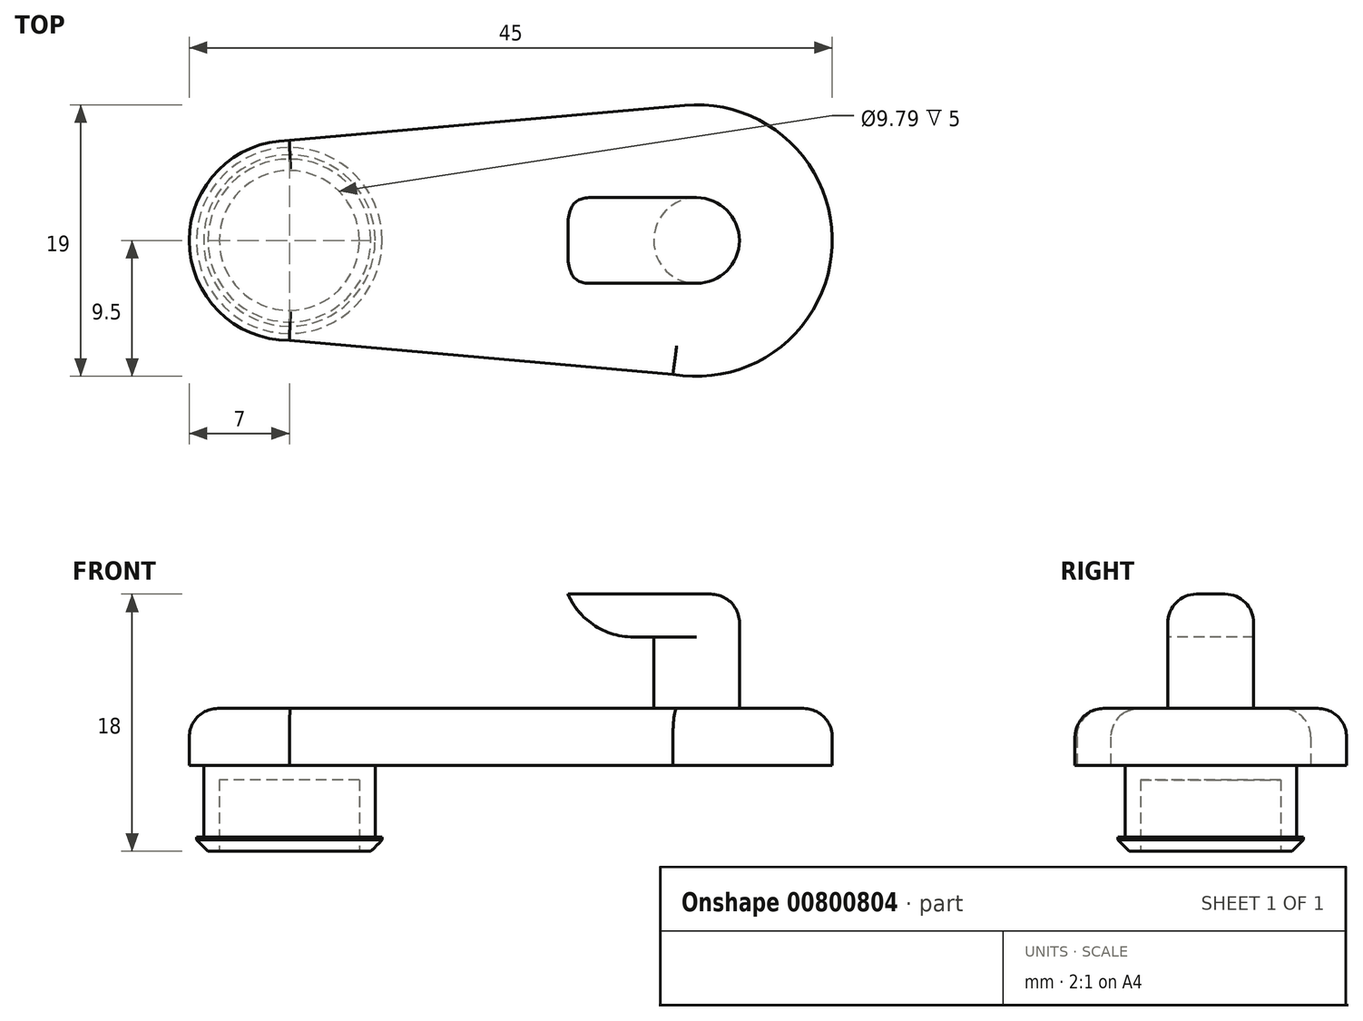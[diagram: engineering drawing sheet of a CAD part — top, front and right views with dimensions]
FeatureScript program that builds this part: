
annotation { "Feature Type Name" : "Feature", "Feature Type Description" : "" }
export const myFeature = defineFeature(function(context is Context, id is Id, definition is map)
    precondition{}
    {
        {
            var Q0;
            Q0=qCreatedBy(makeId("Top.planeOp"),FACE);
            var sketch = newSketch(context, id + "F0", { "sketchPlane" : qUnion([Q0])});
            skCircle(sketch, "E0", {"center": v(0, 0) * mm, "radius": 6 * mm});
            skLineSegment(sketch, "E1", {"start": v(0, 0) * mm, "end": v(-6, 0) * mm, "construction": true});
            skLineSegment(sketch, "E2", {"start": v(-7, 0) * mm, "end": v(-6, 0) * mm, "construction": true});
            skArc(sketch, "E3", {"start": v(0, 7) * mm, "mid": v(-7, 0) * mm, "end": v(0, -7) * mm});
            skLineSegment(sketch, "E4", {"start": v(0, 0) * mm, "end": v(38, 0) * mm, "construction": true});
            skLineSegment(sketch, "E5", {"start": v(25.33, 0) * mm, "end": v(38, 0) * mm, "construction": true});
            skLineSegment(sketch, "E6", {"start": v(31.67, 8.18) * mm, "end": v(31.67, 8.96) * mm, "construction": true});
            skLineSegment(sketch, "E7", {"start": v(25.33, 0) * mm, "end": v(31.67, 0) * mm, "construction": true});
            skLineSegment(sketch, "E8", {"start": v(28.5, 0) * mm, "end": v(28.5, 5.13) * mm, "construction": true});
            skCircle(sketch, "E9", {"center": v(28.5, 0) * mm, "radius": 3 * mm});
            skArc(sketch, "E10", {"start": v(26.85, -9.35) * mm, "mid": v(38, -0.4) * mm, "end": v(27.66, 9.46) * mm});
            skLineSegment(sketch, "E11", {"start": v(0, 7) * mm, "end": v(28.5, 9.54) * mm});
            skLineSegment(sketch, "E12", {"start": v(0, -7) * mm, "end": v(28.5, -9.5) * mm});
            skLineSegment(sketch, "E13", {"start": v(28.5, 0) * mm, "end": v(38, 0) * mm, "construction": true});
            skCircle(sketch, "E14", {"center": v(0, 0) * mm, "radius": 4.9 * mm});
            skLineSegment(sketch, "E15", {"start": v(28.5, 9.54) * mm, "end": v(28.5, -9.5) * mm, "construction": true});
            skPoint(sketch, "E16.start.orphan", {"position": v(12.67, 0) * mm});
            skSolve(sketch);
        }
        {
            var Q0;
            Q0 = qSketchRegion(id + "F0", true);
            extrude(context, id + "F1", {"entities" : qUnion([Q0]), "depth" : 10 * mm, "offsetDistance" : 25 * mm, "hasSecondDirection" : true, "secondDirectionOppositeDirection" : true, "secondDirectionDepth" : -6 * mm});
        }
        {
            var Q0;
            Q0=makeQuery(id+"F1.opExtrude","CAP_EDGE",EDGE,{"disambiguationData":[OSD([sQuery(id+"F0.wireOp",EDGE,"E3")])],"isStart":false});
            var Q1;
            Q1=makeQuery(id+"F1.opExtrude","CAP_EDGE",EDGE,{"disambiguationData":[OSD([sQuery(id+"F0.wireOp",EDGE,"E12")])],"isStart":false});
            var Q2;
            Q2=makeQuery(id+"F1.opExtrude","CAP_EDGE",EDGE,{"disambiguationData":[OSD([sQuery(id+"F0.wireOp",EDGE,"E10")])],"isStart":false});
            var Q3;
            Q3=makeQuery(id+"F1.opExtrude","CAP_EDGE",EDGE,{"disambiguationData":[OSD([sQuery(id+"F0.wireOp",EDGE,"E11")])],"isStart":false});
            fillet(context, id + "F2", {"entities" : qUnion([Q0, Q1, Q2, Q3]), "radius" : 2 * mm, "tangentPropagation" : true, "allowEdgeOverflow" : false});
        }
        {
            var Q0;
            Q0=makeQuery(id+"F0.imprint","IMPRINT",FACE,{"disambiguationData":[TD([[makeQuery(id+"F0.imprint","IMPRINT",EDGE,{"derivedFrom":sQuery(id+"F0.wireOp",EDGE,"E9")}),1.0]])]});
            extrude(context, id + "F3", {"entities" : qUnion([Q0]), "operationType" : NewBodyOperationType.ADD, "depth" : 15 * mm, "offsetDistance" : 25 * mm, "hasSecondDirection" : true, "secondDirectionOppositeDirection" : true, "secondDirectionDepth" : -6 * mm});
        }
        {
            var Q0;
            Q0=makeQuery(id+"F0.imprint","IMPRINT",FACE,{"disambiguationData":[TD([[makeQuery(id+"F0.imprint","IMPRINT",EDGE,{"derivedFrom":sQuery(id+"F0.wireOp",EDGE,"E0")}),1.0]])]});
            var Q1;
            Q1=makeQuery(id+"F0.imprint","IMPRINT",FACE,{"disambiguationData":[TD([[makeQuery(id+"F0.imprint","IMPRINT",EDGE,{"derivedFrom":sQuery(id+"F0.wireOp",EDGE,"E14")}),1.0]])]});
            extrude(context, id + "F4", {"entities" : qUnion([Q0, Q1]), "operationType" : NewBodyOperationType.ADD, "depth" : 10 * mm, "offsetDistance" : 25 * mm});
        }
        {
            var Q0;
            Q0=makeQuery(id+"F0.imprint","IMPRINT",FACE,{"disambiguationData":[TD([[makeQuery(id+"F0.imprint","IMPRINT",EDGE,{"derivedFrom":sQuery(id+"F0.wireOp",EDGE,"E0")}),1.0]])]});
            var sketch = newSketch(context, id + "F5", { "sketchPlane" : qUnion([Q0])});
            skLineSegment(sketch, "E17", {"start": v(0, 0) * mm, "end": v(5.3, 0) * mm, "construction": true});
            skLineSegment(sketch, "E18", {"start": v(5.3, 0) * mm, "end": v(6.5, 0) * mm, "construction": true});
            skCircle(sketch, "E19", {"center": v(0, 0) * mm, "radius": 6.5 * mm});
            skSolve(sketch);
        }
        {
            var Q0;
            Q0=makeQuery(id+"F5.imprint","IMPRINT",FACE,{"disambiguationData":[TD([[makeQuery(id+"F5.imprint","IMPRINT",EDGE,{"derivedFrom":sQuery(id+"F5.wireOp",EDGE,"E19")}),1.0]])]});
            extrude(context, id + "F6", {"entities" : qUnion([Q0]), "operationType" : NewBodyOperationType.ADD, "depth" : 1 * mm, "offsetDistance" : 25 * mm});
        }
        {
            var Q0;
            Q0=makeQuery(id+"F6.opExtrude","CAP_EDGE",EDGE,{"disambiguationData":[OSD([sQuery(id+"F5.wireOp",EDGE,"E19")])],"isStart":true});
            chamfer(context, id + "F7", {"entities" : qUnion([Q0]), "width" : 0.8 * mm, "tangentPropagation" : true});
        }
        {
            var Q0;
            Q0=makeQuery(id+"F3.opExtrude","CAP_FACE",FACE,{"disambiguationData":[OSD([sQuery(id+"F0.wireOp",EDGE,"E9")])],"isStart":false});
            var sketch = newSketch(context, id + "F8", { "sketchPlane" : qUnion([Q0])});
            skLineSegment(sketch, "E20", {"start": v(28.5, 0) * mm, "end": v(25.5, 0) * mm, "construction": true});
            skLineSegment(sketch, "E21", {"start": v(25.5, 0) * mm, "end": v(28.5, 0) * mm, "construction": true});
            skLineSegment(sketch, "E22", {"start": v(18.53, 0) * mm, "end": v(25.5, 0) * mm, "construction": true});
            skLineSegment(sketch, "E23", {"start": v(31.5, 0.1) * mm, "end": v(36.48, 0.1) * mm, "construction": true});
            skLineSegment(sketch, "E24", {"start": v(28.5, 3) * mm, "end": v(56.17, 3) * mm, "construction": true});
            skLineSegment(sketch, "E25", {"start": v(31.5, 0) * mm, "end": v(31.5, -4.88) * mm, "construction": true});
            skLineSegment(sketch, "E26", {"start": v(31.5, 0) * mm, "end": v(31.5, 6.6) * mm, "construction": true});
            skLineSegment(sketch, "E27.bottom", {"start": v(31.5, 3) * mm, "end": v(19.5, 3) * mm});
            skLineSegment(sketch, "E27.top", {"start": v(31.5, -3) * mm, "end": v(19.5, -3) * mm});
            skLineSegment(sketch, "E27.left", {"start": v(31.5, 3) * mm, "end": v(31.5, -3) * mm});
            skLineSegment(sketch, "E27.right", {"start": v(19.5, 3) * mm, "end": v(19.5, -3) * mm});
            skPoint(sketch, "E27.middle", {"position": v(25.5, 0) * mm});
            skSolve(sketch);
        }
        {
            var Q0;
            {var subQ0=sQuery(id+"F8.wireOp",EDGE,"E27.right");Q0=makeQuery(id+"F8.imprint","IMPRINT",FACE,{"disambiguationData":[TD([[makeQuery(id+"F8.imprint","IMPRINT",EDGE,{"derivedFrom":subQ0}),1.0]])]});}
            var Q1;
            {var subQ0=makeQuery(id+"F3.opExtrude","CAP_EDGE",EDGE,{"disambiguationData":[OSD([sQuery(id+"F0.wireOp",EDGE,"E9")])],"isStart":false});var subQ1=makeQuery(id+"F8.imprint","INTERSECT",VERTEX,{"derivedFrom":[subQ0,sQuery(id+"F8.wireOp",EDGE,"E27.bottom")]});Q1=makeQuery(id+"F8.imprint","IMPRINT",FACE,{"disambiguationData":[TD([[makeQuery(id+"F8.imprint","IMPRINT",EDGE,{"disambiguationData":[TD([[subQ1,-1.0]])],"derivedFrom":subQ0}),1.0]])]});}
            extrude(context, id + "F9", {"entities" : qUnion([Q0, Q1]), "operationType" : NewBodyOperationType.ADD, "depth" : 3 * mm, "offsetDistance" : 25 * mm});
        }
        {
            var Q0;
            Q0=makeQuery(id+"F9.opExtrude","CAP_EDGE",EDGE,{"disambiguationData":[OSD([sQuery(id+"F8.wireOp",EDGE,"E27.right")])],"isStart":true});
            fillet(context, id + "F10", {"entities" : qUnion([Q0]), "radius" : 5 * mm, "tangentPropagation" : true, "allowEdgeOverflow" : false});
        }
        {
            var Q0;
            {var subQ0=sQuery(id+"F0.wireOp",EDGE,"XsBtpHIO-92i5-3BHP-AfYB-fZm0eGe0ryfA.top");var subQ1=sQuery(id+"F0.wireOp",EDGE,"E14");var subQ2=makeQuery(id+"F0.imprint","INTERSECT",VERTEX,{"disambiguationData":[OD(0.0)],"derivedFrom":[subQ1,subQ0]});Q0=makeQuery(id+"F0.imprint","IMPRINT",FACE,{"disambiguationData":[TD([[makeQuery(id+"F0.imprint","IMPRINT",EDGE,{"disambiguationData":[TD([[subQ2,-1.0]])],"derivedFrom":subQ1}),1.0]])]});}
            var Q1;
            {var subQ0=sQuery(id+"F0.wireOp",EDGE,"lAm7fckA-uWJb-f2yY-rN9Z-U4NhKii0mZ3q.right");var subQ1=sQuery(id+"F0.wireOp",EDGE,"E14");var subQ2=makeQuery(id+"F0.imprint","INTERSECT",VERTEX,{"disambiguationData":[OD(0.0)],"derivedFrom":[subQ1,subQ0]});Q1=makeQuery(id+"F0.imprint","IMPRINT",FACE,{"disambiguationData":[TD([[makeQuery(id+"F0.imprint","IMPRINT",EDGE,{"disambiguationData":[TD([[subQ2,-1.0]])],"derivedFrom":subQ1}),1.0]])]});}
            var Q2;
            {var subQ0=sQuery(id+"F0.wireOp",EDGE,"XsBtpHIO-92i5-3BHP-AfYB-fZm0eGe0ryfA.bottom");var subQ1=sQuery(id+"F0.wireOp",EDGE,"E14");var subQ2=makeQuery(id+"F0.imprint","INTERSECT",VERTEX,{"disambiguationData":[OD(1.0)],"derivedFrom":[subQ1,subQ0]});Q2=makeQuery(id+"F0.imprint","IMPRINT",FACE,{"disambiguationData":[TD([[makeQuery(id+"F0.imprint","IMPRINT",EDGE,{"disambiguationData":[TD([[subQ2,-1.0]])],"derivedFrom":subQ1}),1.0]])]});}
            var Q3;
            {var subQ0=sQuery(id+"F0.wireOp",EDGE,"lAm7fckA-uWJb-f2yY-rN9Z-U4NhKii0mZ3q.left");var subQ1=sQuery(id+"F0.wireOp",EDGE,"E14");var subQ2=makeQuery(id+"F0.imprint","INTERSECT",VERTEX,{"disambiguationData":[OD(0.0)],"derivedFrom":[subQ1,subQ0]});Q3=makeQuery(id+"F0.imprint","IMPRINT",FACE,{"disambiguationData":[TD([[makeQuery(id+"F0.imprint","IMPRINT",EDGE,{"disambiguationData":[TD([[subQ2,-1.0]])],"derivedFrom":subQ1}),1.0]])]});}
            var Q4;
            {var subQ0=sQuery(id+"F0.wireOp",EDGE,"lAm7fckA-uWJb-f2yY-rN9Z-U4NhKii0mZ3q.left");var subQ1=sQuery(id+"F0.wireOp",EDGE,"E14");var subQ2=makeQuery(id+"F0.imprint","INTERSECT",VERTEX,{"disambiguationData":[OD(0.0)],"derivedFrom":[subQ1,subQ0]});Q4=makeQuery(id+"F0.imprint","IMPRINT",FACE,{"disambiguationData":[TD([[makeQuery(id+"F0.imprint","IMPRINT",EDGE,{"disambiguationData":[TD([[subQ2,1.0]])],"derivedFrom":subQ1}),1.0]])]});}
            var Q5;
            {var subQ0=sQuery(id+"F0.wireOp",EDGE,"lAm7fckA-uWJb-f2yY-rN9Z-U4NhKii0mZ3q.left");var subQ1=sQuery(id+"F0.wireOp",EDGE,"XsBtpHIO-92i5-3BHP-AfYB-fZm0eGe0ryfA.bottom");var subQ2=makeQuery(id+"F0.imprint","INTERSECT",VERTEX,{"derivedFrom":[subQ1,subQ0]});Q5=makeQuery(id+"F0.imprint","IMPRINT",FACE,{"disambiguationData":[TD([[makeQuery(id+"F0.imprint","IMPRINT",EDGE,{"disambiguationData":[TD([[subQ2,-1.0]])],"derivedFrom":subQ1}),1.0]])]});}
            var Q6;
            {var subQ0=sQuery(id+"F0.wireOp",EDGE,"lAm7fckA-uWJb-f2yY-rN9Z-U4NhKii0mZ3q.right");var subQ1=sQuery(id+"F0.wireOp",EDGE,"E14");var subQ2=makeQuery(id+"F0.imprint","INTERSECT",VERTEX,{"disambiguationData":[OD(1.0)],"derivedFrom":[subQ1,subQ0]});Q6=makeQuery(id+"F0.imprint","IMPRINT",FACE,{"disambiguationData":[TD([[makeQuery(id+"F0.imprint","IMPRINT",EDGE,{"disambiguationData":[TD([[subQ2,-1.0]])],"derivedFrom":subQ1}),1.0]])]});}
            var Q7;
            {var subQ0=sQuery(id+"F0.wireOp",EDGE,"lAm7fckA-uWJb-f2yY-rN9Z-U4NhKii0mZ3q.left");var subQ1=sQuery(id+"F0.wireOp",EDGE,"E14");var subQ2=makeQuery(id+"F0.imprint","INTERSECT",VERTEX,{"disambiguationData":[OD(1.0)],"derivedFrom":[subQ1,subQ0]});Q7=makeQuery(id+"F0.imprint","IMPRINT",FACE,{"disambiguationData":[TD([[makeQuery(id+"F0.imprint","IMPRINT",EDGE,{"disambiguationData":[TD([[subQ2,-1.0]])],"derivedFrom":subQ1}),1.0]])]});}
            var Q8;
            {var subQ0=sQuery(id+"F0.wireOp",EDGE,"XsBtpHIO-92i5-3BHP-AfYB-fZm0eGe0ryfA.bottom");var subQ1=sQuery(id+"F0.wireOp",EDGE,"E14");var subQ2=makeQuery(id+"F0.imprint","INTERSECT",VERTEX,{"disambiguationData":[OD(0.0)],"derivedFrom":[subQ1,subQ0]});Q8=makeQuery(id+"F0.imprint","IMPRINT",FACE,{"disambiguationData":[TD([[makeQuery(id+"F0.imprint","IMPRINT",EDGE,{"disambiguationData":[TD([[subQ2,1.0]])],"derivedFrom":subQ1}),1.0]])]});}
            extrude(context, id + "F11", {"entities" : qUnion([Q0, Q1, Q2, Q3, Q4, Q5, Q6, Q7, Q8]), "operationType" : NewBodyOperationType.REMOVE, "oppositeDirection" : true, "depth" : -5 * mm, "offsetDistance" : 25 * mm});
        }
        {
            var Q0;
            Q0=makeQuery(id+"F4.opExtrude","CAP_EDGE",EDGE,{"disambiguationData":[OSD([sQuery(id+"F0.wireOp",EDGE,"E0")])],"isStart":false});
            fillet(context, id + "F12", {"entities" : qUnion([Q0]), "radius" : 2 * mm, "tangentPropagation" : true, "allowEdgeOverflow" : false});
        }
        {
            var Q0;
            Q0=makeQuery(id+"F9.opExtrude","CAP_EDGE",EDGE,{"disambiguationData":[OSD([sQuery(id+"F0.wireOp",EDGE,"E9")])],"isStart":false});
            fillet(context, id + "F13", {"entities" : qUnion([Q0]), "radius" : 2 * mm, "tangentPropagation" : true, "allowEdgeOverflow" : false});
        }
    });
